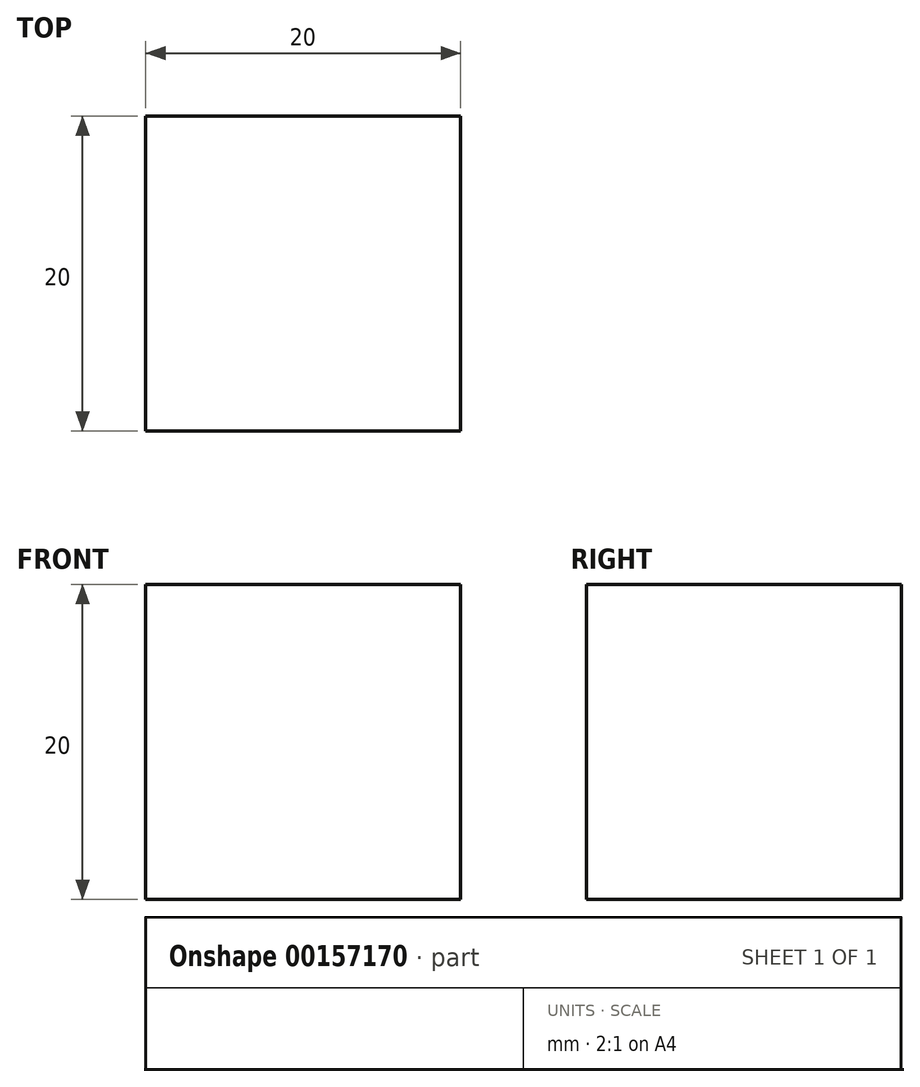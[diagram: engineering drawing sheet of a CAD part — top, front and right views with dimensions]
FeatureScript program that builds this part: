
annotation { "Feature Type Name" : "Feature", "Feature Type Description" : "" }
export const myFeature = defineFeature(function(context is Context, id is Id, definition is map)
    precondition{}
    {
        {
            var Q0;
            Q0=qCreatedBy(makeId("Top.planeOp"),FACE);
            var sketch = newSketch(context, id + "F0", { "sketchPlane" : qUnion([Q0])});
            skLineSegment(sketch, "E0.bottom", {"start": v(10, 10) * mm, "end": v(-10, 10) * mm});
            skLineSegment(sketch, "E0.top", {"start": v(10, -10) * mm, "end": v(-10, -10) * mm});
            skLineSegment(sketch, "E0.left", {"start": v(10, 10) * mm, "end": v(10, -10) * mm});
            skLineSegment(sketch, "E0.right", {"start": v(-10, 10) * mm, "end": v(-10, -10) * mm});
            skPoint(sketch, "E0.middle", {"position": v(0, 0) * mm});
            skSolve(sketch);
        }
        {
            var Q0;
            Q0=makeQuery(id+"F0.imprint","IMPRINT",FACE,{"disambiguationData":[TD([[makeQuery(id+"F0.imprint","IMPRINT",EDGE,{"derivedFrom":sQuery(id+"F0.wireOp",EDGE,"E0.bottom")}),1.0]])]});
            extrude(context, id + "F1", {"entities" : qUnion([Q0]), "depth" : 20 * mm});
        }
    });
